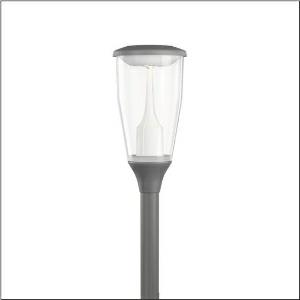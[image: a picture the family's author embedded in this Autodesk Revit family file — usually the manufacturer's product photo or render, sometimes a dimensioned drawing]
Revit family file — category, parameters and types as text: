
# Revit family: dl_11_iq___st1_2a_5xa5575af14hp00022_5e00
name_source: partatom
category: Lighting Fixtures
units: mm (PartAtom-declared; Revit-internal decimal feet)

## family parameters
Cut with Voids When Loaded = No
Host = Face
Light Source = No
Part Type = Normal
Room Calculation Point = No
Round Connector Dimension = Use Diameter
Shared = No

## types (1)
- --- (1 x LED, 4000 lm, 33.6 W, 2200K)
    Apparent Load = 34 VA
    CIE Flux Codes = 23 60 93 95 100
    Color Rendering = 70
    Color Temperature = 2200K
    Default Elevation = 1800 mm
    Description = DL 11 iQ, mast luminaire, Module 540 iQ-SR, primary light control with 3 zone facetted reflector, of plastic, silver coated, highly specular, structured, primary optical cover: cover, of PMMA, transparent, light distribution: ST1.2a, light emission: direct distribution, primary light characteristic: asymmetric, installation type: post-top, LED, High Power LED, rated luminous flux: 4.000lm, luminous efficacy: 119lm/W, light colour: 722, colour temperature: 2200K, control gear: iQ Street-Remote, control: Street-Remote, Auto-Match, Temp-Guard, Lumen-Switch, Night-Set, Smart-Wire, Light-Fading, Desk-Remote (wireless, voltage-free reading and setting of iQ features in the workshop via application-optimized NFC function/RFID function), optimised constant luminous flux control (CLO 2.0), mains connection: 220..240V, AC, 50/60Hz, connection cable pre-assembled, cable length: 5,5m, start of lifetime: 34W, end of service life: 36W, reduction: 15W, luminaire housing, upper part, of diecast aluminium, coated, Siteco® metallic grey (DB 702S), spigot size: 76mm (post-top), mounting height: 3..5m, post-top mast mounting element, of diecast aluminium, coated, Siteco® metallic grey (DB 702S), Module 540 iQ-SR, traffic white (RAL 9016), equipment: Power, protection rating (complete): IP66, insulation class (complete): insulation class II (safety insulation), certification: CE, ENEC, ENEC+, VDE, impact resistance: IK07, packaging unit: 1 piece

Light Distribution: ST1.2a
    Height = 665 mm
    Lamp = 1 x LED
    Lamp Light Flux = 4000 lm
    Lamp Power = 33.6 W
    Lamp count = 1
    Length = 334 mm
    Luminous efficacy = 119 lm/W
    Manufacturer = Siteco
    ModVariant = No
    Model = 5XA5575AF14HP00022
    Number of Poles = 1
    OnlyDefault = Yes
    Power Factor = 1
    Product Name = DL 11 iQ | ST1.2a
    Product group = mast luminaire | pylon top
    ProductGroupID = 6100
    Protection Class = Protection class II
    Protection Degree = IP 66
    RLX_Detail_Level = 1
    RLX_Emergency_Light_Flux = 0 lm
    RLX_Emergency_Type = 0
    RLX_Emergency_Type_DB = No
    RlxData = <blob elided: 141565 chars, md5=85aba696>
    Socket = socket
    Standby Power = 0 W
    System Light Flux = 4000 lm
    System Power = 34 W
    Type Comments = factory setting: luminous flux: 100 % | dim-lin: 254 | 695 mA
    Type Image = l_1258354.jpg
    URL = http://relux.com
    VarID = @adj_053595
    Voltage = 0 V
    Weight = 0.00 kg
    Width = 0 mm  [stored 0 ft]

note: [stored X ft] marks values corroborated as IEEE doubles in the binary element streams (Revit-internal decimal feet)

## geometry (parser evidence)
native form markers: Blend x4, Sweep x10
no freeform markers — native parametric forms only
